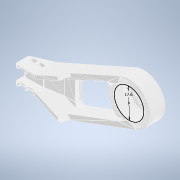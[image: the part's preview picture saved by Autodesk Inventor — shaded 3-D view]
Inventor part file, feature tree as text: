
AUTODESK INVENTOR PART (.ipt)
format: ipt  version: 2020 (Build 240168000, 168)  size: 219,648 bytes
history: native  units: in
note: dims shown in document units (in); Inventor stores cm internally (conversion verified against a paired STEP export)
features: other x2, sketch x1
ambient origin geometry x8: Origin, YZ Plane, XZ Plane, XY Plane, X Axis, Y Axis, Z Axis, Center Point
feature tree (3):
  other  "Wire_Strain_Relief_Bracket_Base"
  sketch  "Sketch1"  dims[d0=0.6929in]
  other  "MeshFeature1"
